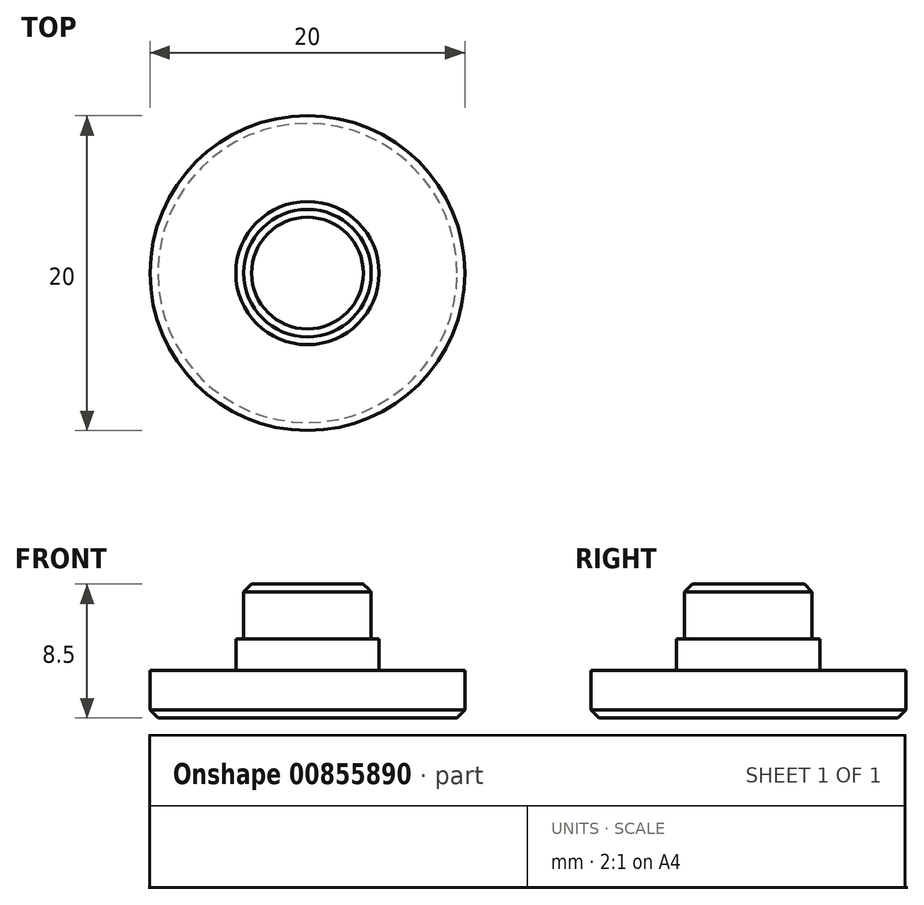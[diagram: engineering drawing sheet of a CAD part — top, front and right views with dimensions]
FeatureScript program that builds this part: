
annotation { "Feature Type Name" : "Feature", "Feature Type Description" : "" }
export const myFeature = defineFeature(function(context is Context, id is Id, definition is map)
    precondition{}
    {
        {
            var Q0;
            Q0=qCreatedBy(makeId("Top.planeOp"),FACE);
            var sketch = newSketch(context, id + "F0", { "sketchPlane" : qUnion([Q0])});
            skCircle(sketch, "E0", {"center": v(0, 0) * mm, "radius": 10 * mm});
            skSolve(sketch);
        }
        {
            var Q0;
            Q0=qSketchRegion(id+"F0",true);
            extrude(context, id + "F1", {"entities" : qUnion([Q0]), "depth" : 3 * mm, "offsetDistance" : 25 * mm});
        }
        {
            var Q0;
            Q0=makeQuery(id+"F1.opExtrude","CAP_FACE",FACE,{"disambiguationData":[OSD([sQuery(id+"F0.wireOp",EDGE,"E0")])],"isStart":false});
            var sketch = newSketch(context, id + "F2", { "sketchPlane" : qUnion([Q0])});
            skCircle(sketch, "E1", {"center": v(0, 0) * mm, "radius": 4.05 * mm});
            skSolve(sketch);
        }
        {
            var Q0;
            Q0=qSketchRegion(id+"F2",true);
            extrude(context, id + "F3", {"entities" : qUnion([Q0]), "operationType" : NewBodyOperationType.ADD, "depth" : 5.5 * mm, "offsetDistance" : 25 * mm});
        }
        {
            var Q0;
            Q0=makeQuery(id+"F3.opExtrude","CAP_EDGE",EDGE,{"disambiguationData":[OSD([sQuery(id+"F2.wireOp",EDGE,"E1")])],"isStart":false});
            var Q1;
            Q1=makeQuery(id+"F1.opExtrude","CAP_EDGE",EDGE,{"disambiguationData":[OSD([sQuery(id+"F0.wireOp",EDGE,"E0")])],"isStart":true});
            chamfer(context, id + "F4", {"entities" : qUnion([Q0, Q1]), "width" : 0.5 * mm, "tangentPropagation" : true});
        }
        {
            var Q0;
            Q0=makeQuery(id+"F1.opExtrude","CAP_FACE",FACE,{"disambiguationData":[OSD([sQuery(id+"F0.wireOp",EDGE,"E0")])],"isStart":false});
            var sketch = newSketch(context, id + "F5", { "sketchPlane" : qUnion([Q0])});
            skCircle(sketch, "E2", {"center": v(0, 0) * mm, "radius": 4.55 * mm});
            skSolve(sketch);
        }
        {
            var Q0;
            Q0=qSketchRegion(id+"F5",true);
            extrude(context, id + "F6", {"entities" : qUnion([Q0]), "operationType" : NewBodyOperationType.ADD, "depth" : 2 * mm, "offsetDistance" : 25 * mm});
        }
    });
